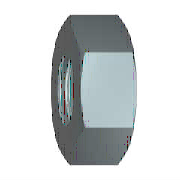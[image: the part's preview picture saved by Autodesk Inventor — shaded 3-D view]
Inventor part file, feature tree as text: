
AUTODESK INVENTOR PART (.ipt)
format: ipt  version: 2023 (Build 270158000, 158)  size: 165,376 bytes
history: native  units: mm (DEFAULTED — no unit token found)
features: sketch x3, other x2, extrude x1, hole x1, plane x1
ambient origin geometry x7: Origin, YZ Plane, XZ Plane, X Axis, Y Axis, Z Axis, Center Point
bodies: Solid1 (feature_tree)
feature tree (8):
  extrude  "Базовый элемент"  Depth=18.475209mm
  other  "Фаска1"
  hole  "Резьба"  [1 undecoded]
  other  "Work Axis1"
  plane  "Work Plane1"
  sketch  "Эскиз1"
  sketch  "Эскиз2"
  sketch  "Эскиз3"
note: 1 required parameter value undecoded (feature->parameter linkage not recoverable at this tier; creation-order binding heuristic only, values carry confidence <= 0.55)
